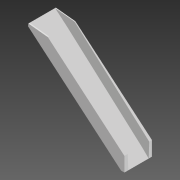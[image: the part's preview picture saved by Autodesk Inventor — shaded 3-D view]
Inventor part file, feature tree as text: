
AUTODESK INVENTOR PART (.ipt)
format: ipt  version: 2020.4 (Build 244396010, 396A)  size: 98,816 bytes
history: native  units: in
note: dims shown in document units (in); Inventor stores cm internally (conversion verified against a paired STEP export)
features: reference x7, other x3, extrude x2, sketch x2, plane x1
ambient origin geometry x8: Origin, YZ Plane, XZ Plane, XY Plane, X Axis, Y Axis, Z Axis, Center Point
bodies: Solid1 (feature_tree)
feature tree (15):
  extrude  "Extrusion1"  Depth=1.75in TaperAngle=0.0deg
  sketch  "Sketch2"
  plane  "Work Plane1"
  extrude  "Extrusion2"  [1 undecoded]
  sketch  "Sketch1"  dims[d4=1.75in d5=0.0in d6=1.0in d7=0.0in]
  reference  "Reference1"
  reference  "Reference2"
  reference  "Reference3"
  reference  "Reference4"
  reference  "Reference5"
  reference  "Reference6"
  reference  "Reference7"
  other  "<userpath>\Desktop\hybrid\src\Hybrid.iam"
  other  "Hybrid.iam"
  other  "Hybrid:1"
note: 1 required parameter value undecoded (feature->parameter linkage not recoverable at this tier; creation-order binding heuristic only, values carry confidence <= 0.55)
